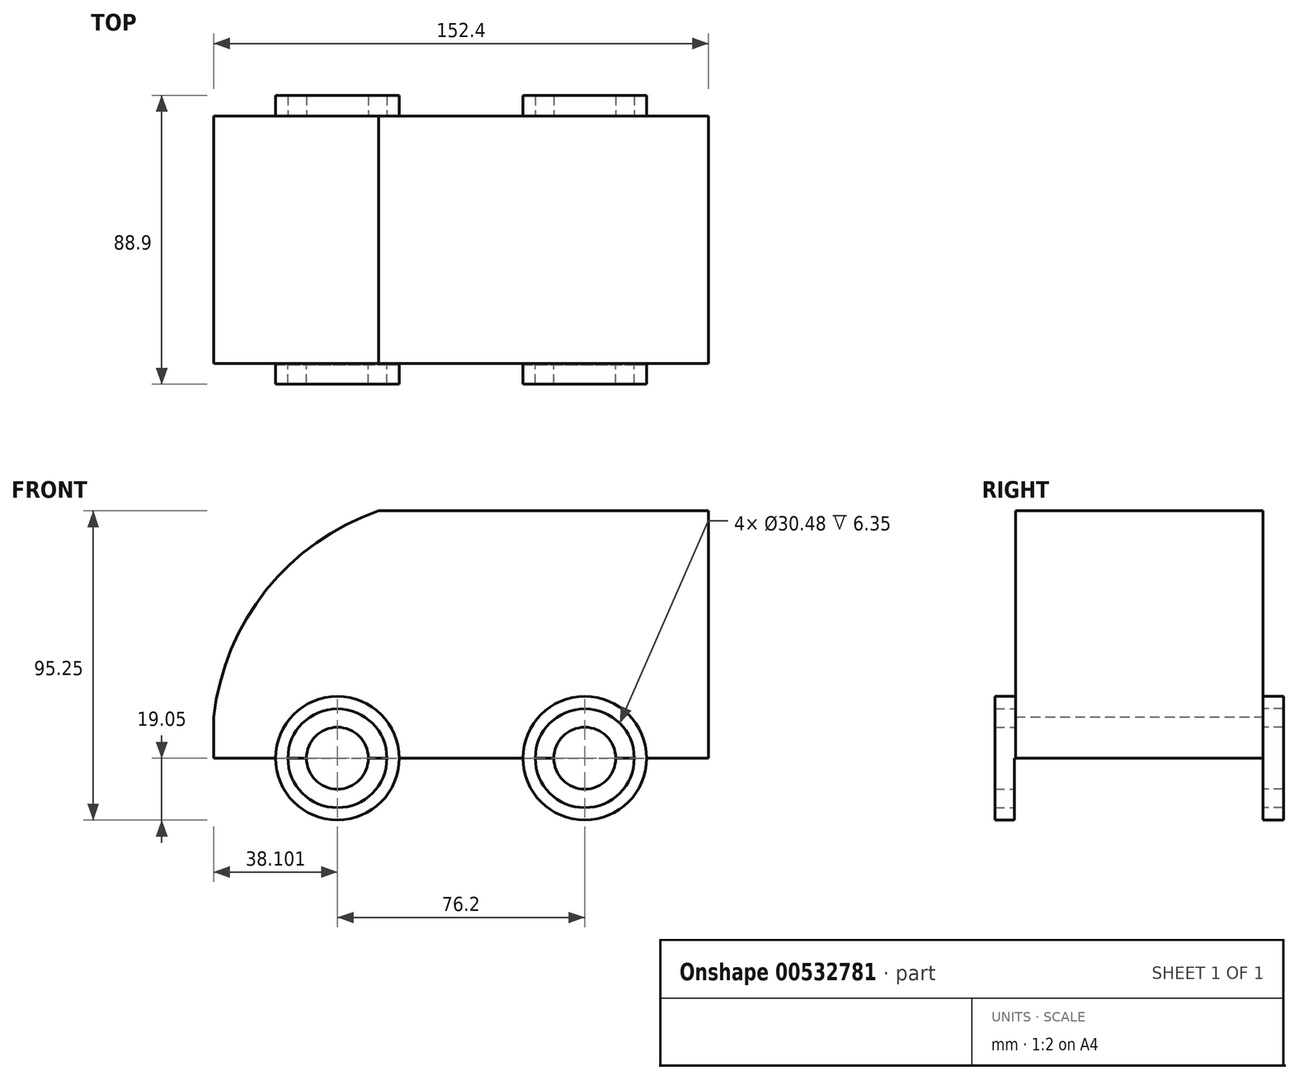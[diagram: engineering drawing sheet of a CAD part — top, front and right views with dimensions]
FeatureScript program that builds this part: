
annotation { "Feature Type Name" : "Feature", "Feature Type Description" : "" }
export const myFeature = defineFeature(function(context is Context, id is Id, definition is map)
    precondition{}
    {
        {
            var Q0;
            Q0=qCreatedBy(makeId("Front.planeOp"),FACE);
            var sketch = newSketch(context, id + "F0", { "sketchPlane" : qUnion([Q0])});
            skLineSegment(sketch, "E0", {"start": v(101.96, 0) * mm, "end": v(101.96, 76.2) * mm});
            skLineSegment(sketch, "E1", {"start": v(101.96, 76.2) * mm, "end": v(0.36, 76.2) * mm});
            skLineSegment(sketch, "E2", {"start": v(-50.44, 12.7) * mm, "end": v(-50.44, 0) * mm});
            skPoint(sketch, "E3.visualSharp", {"position": v(-50.44, 76.2) * mm});
            skPoint(sketch, "E4.third.point", {"position": v(59.34, 39.94) * mm});
            skArc(sketch, "E5", {"start": v(0.36, 76.2) * mm, "mid": v(-34.25, 51.82) * mm, "end": v(-50.44, 12.7) * mm});
            skPoint(sketch, "E5.third.point", {"position": v(92.28, -31.17) * mm});
            skLineSegment(sketch, "E6", {"start": v(-50.44, 0) * mm, "end": v(-12.34, 0) * mm});
            skLineSegment(sketch, "E7", {"start": v(101.96, 0) * mm, "end": v(63.86, 0) * mm});
            skCircle(sketch, "E8", {"center": v(-12.34, 0) * mm, "radius": 19.05 * mm});
            skCircle(sketch, "E9", {"center": v(63.86, 0) * mm, "radius": 19.05 * mm});
            skLineSegment(sketch, "E10", {"start": v(-12.34, 0) * mm, "end": v(63.86, 0) * mm});
            skSolve(sketch);
        }
        {
            var Q0;
            Q0 = qSketchRegion(id + "F0", true);
            extrude(context, id + "F1", {"entities" : qUnion([Q0]), "depth" : 76.2 * mm, "offsetDistance" : 25.4 * mm});
        }
        {
            var Q0;
            Q0=makeQuery(id+"F1.opExtrude","CAP_FACE",FACE,{"disambiguationData":[OSD([sQuery(id+"F0.wireOp",EDGE,"E0"),sQuery(id+"F0.wireOp",EDGE,"E1"),sQuery(id+"F0.wireOp",EDGE,"E2"),sQuery(id+"F0.wireOp",EDGE,"E5"),sQuery(id+"F0.wireOp",EDGE,"E6"),sQuery(id+"F0.wireOp",EDGE,"E7"),sQuery(id+"F0.wireOp",EDGE,"E8"),sQuery(id+"F0.wireOp",EDGE,"E9"),sQuery(id+"F0.wireOp",EDGE,"E10")])],"isStart":false});
            var sketch = newSketch(context, id + "F2", { "sketchPlane" : qUnion([Q0])});
            skCircle(sketch, "E11", {"center": v(-12.34, 0) * mm, "radius": 9.53 * mm});
            skCircle(sketch, "E12", {"center": v(-12.34, 0) * mm, "radius": 19.05 * mm});
            skCircle(sketch, "E13", {"center": v(63.86, 0) * mm, "radius": 19.05 * mm});
            skCircle(sketch, "E14", {"center": v(63.86, 0) * mm, "radius": 9.53 * mm});
            skCircle(sketch, "E15", {"center": v(-12.34, 0) * mm, "radius": 15.24 * mm});
            skCircle(sketch, "E16", {"center": v(63.86, 0) * mm, "radius": 15.24 * mm});
            skSolve(sketch);
        }
        {
            var Q0;
            Q0=makeQuery(id+"F2.imprint","IMPRINT",FACE,{"disambiguationData":[TD([[makeQuery(id+"F2.imprint","IMPRINT",EDGE,{"derivedFrom":sQuery(id+"F2.wireOp",EDGE,"E16")}),-1.0]])]});
            var Q1;
            Q1=makeQuery(id+"F2.imprint","IMPRINT",FACE,{"disambiguationData":[TD([[makeQuery(id+"F2.imprint","IMPRINT",EDGE,{"derivedFrom":sQuery(id+"F2.wireOp",EDGE,"E15")}),-1.0]])]});
            extrude(context, id + "F3", {"entities" : qUnion([Q0, Q1]), "operationType" : NewBodyOperationType.ADD, "depth" : 6.35 * mm, "offsetDistance" : 25.4 * mm});
        }
        {
            var Q0;
            Q0=makeQuery(id+"F2.imprint","IMPRINT",FACE,{"disambiguationData":[TD([[makeQuery(id+"F2.imprint","IMPRINT",EDGE,{"derivedFrom":sQuery(id+"F2.wireOp",EDGE,"E14")}),1.0]])]});
            var Q1;
            Q1=makeQuery(id+"F2.imprint","IMPRINT",FACE,{"disambiguationData":[TD([[makeQuery(id+"F2.imprint","IMPRINT",EDGE,{"derivedFrom":sQuery(id+"F2.wireOp",EDGE,"E11")}),1.0]])]});
            extrude(context, id + "F4", {"entities" : qUnion([Q0, Q1]), "operationType" : NewBodyOperationType.ADD, "depth" : 6.35 * mm, "offsetDistance" : 25.4 * mm});
        }
        {
            var Q0;
            Q0=makeQuery(id+"F1.opExtrude","CAP_FACE",FACE,{"disambiguationData":[OSD([sQuery(id+"F0.wireOp",EDGE,"E0"),sQuery(id+"F0.wireOp",EDGE,"E1"),sQuery(id+"F0.wireOp",EDGE,"E2"),sQuery(id+"F0.wireOp",EDGE,"E5"),sQuery(id+"F0.wireOp",EDGE,"E6"),sQuery(id+"F0.wireOp",EDGE,"E7"),sQuery(id+"F0.wireOp",EDGE,"E8"),sQuery(id+"F0.wireOp",EDGE,"E9"),sQuery(id+"F0.wireOp",EDGE,"E10")])],"isStart":true});
            var sketch = newSketch(context, id + "F5", { "sketchPlane" : qUnion([Q0])});
            skCircle(sketch, "E17", {"center": v(-63.86, 0) * mm, "radius": 19.05 * mm});
            skCircle(sketch, "E18", {"center": v(12.34, 0) * mm, "radius": 19.05 * mm});
            skCircle(sketch, "E19", {"center": v(-63.86, 0) * mm, "radius": 9.53 * mm});
            skCircle(sketch, "E20", {"center": v(12.34, 0) * mm, "radius": 9.53 * mm});
            skCircle(sketch, "E21", {"center": v(-63.86, 0) * mm, "radius": 15.24 * mm});
            skCircle(sketch, "E22", {"center": v(12.34, 0) * mm, "radius": 15.24 * mm});
            skSolve(sketch);
        }
        {
            var Q0;
            {var subQ0=sQuery(id+"F5.wireOp",EDGE,"E17");Q0=makeQuery(id+"F5.imprint","IMPRINT",FACE,{"disambiguationData":[TD([[makeQuery(id+"F5.imprint","IMPRINT",EDGE,{"disambiguationData":[OD(0.0)],"derivedFrom":subQ0}),1.0]])]});}
            var Q1;
            {var subQ0=sQuery(id+"F5.wireOp",EDGE,"E18");Q1=makeQuery(id+"F5.imprint","IMPRINT",FACE,{"disambiguationData":[TD([[makeQuery(id+"F5.imprint","IMPRINT",EDGE,{"disambiguationData":[OD(0.0)],"derivedFrom":subQ0}),1.0]])]});}
            extrude(context, id + "F6", {"entities" : qUnion([Q0, Q1]), "operationType" : NewBodyOperationType.ADD, "depth" : 6.35 * mm, "offsetDistance" : 25.4 * mm});
        }
        {
            var Q0;
            Q0=makeQuery(id+"F5.imprint","IMPRINT",FACE,{"disambiguationData":[TD([[makeQuery(id+"F5.imprint","IMPRINT",EDGE,{"derivedFrom":sQuery(id+"F5.wireOp",EDGE,"E19")}),1.0]])]});
            var Q1;
            Q1=makeQuery(id+"F5.imprint","IMPRINT",FACE,{"disambiguationData":[TD([[makeQuery(id+"F5.imprint","IMPRINT",EDGE,{"derivedFrom":sQuery(id+"F5.wireOp",EDGE,"E20")}),1.0]])]});
            extrude(context, id + "F7", {"entities" : qUnion([Q0, Q1]), "operationType" : NewBodyOperationType.ADD, "depth" : 6.35 * mm, "offsetDistance" : 25.4 * mm});
        }
        {
            var Q0;
            Q0=makeQuery(id+"F1.opExtrude","SWEPT_FACE",FACE,{"disambiguationData":[OSD([sQuery(id+"F0.wireOp",EDGE,"E10")])]});
            var sketch = newSketch(context, id + "F8", { "sketchPlane" : qUnion([Q0])});
            skLineSegment(sketch, "E23.bottom", {"start": v(-50.8, 76.57) * mm, "end": v(101.74, 76.57) * mm});
            skLineSegment(sketch, "E23.top", {"start": v(-50.8, 0) * mm, "end": v(101.74, 0) * mm});
            skLineSegment(sketch, "E23.left", {"start": v(-50.8, 76.57) * mm, "end": v(-50.8, 0) * mm});
            skLineSegment(sketch, "E23.right", {"start": v(101.74, 76.57) * mm, "end": v(101.74, 0) * mm});
            skSolve(sketch);
        }
        {
            var Q0;
            Q0 = qSketchRegion(id + "F8", true);
            extrude(context, id + "F9", {"entities" : qUnion([Q0]), "operationType" : NewBodyOperationType.REMOVE, "depth" : 25.4 * mm, "offsetDistance" : 25.4 * mm});
        }
    });
